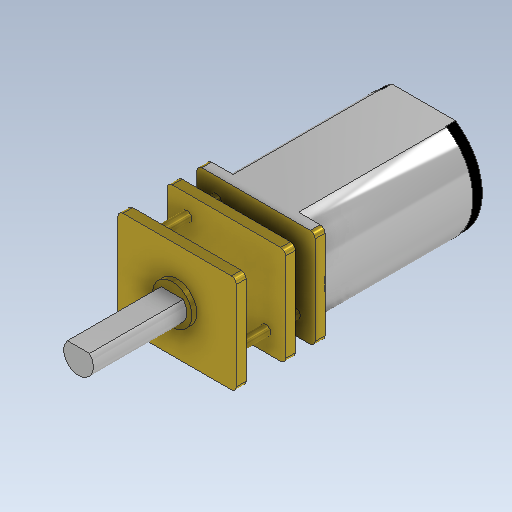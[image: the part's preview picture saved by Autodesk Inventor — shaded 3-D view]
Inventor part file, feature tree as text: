
AUTODESK INVENTOR PART (.ipt)
format: ipt  version: 2020.2 (Build 242310000, 310)  size: 272,896 bytes
history: native  units: mm
features: extrude x11, sketch x10
ambient origin geometry x8: Origin, YZ Plane, XZ Plane, XY Plane, X Axis, Y Axis, Z Axis, Center Point
bodies: Solid1 (feature_tree)
feature tree (21):
  extrude  "Extrusion1"  Depth=5.0mm
  extrude  "Extrusion2"  Depth=15.0mm TaperAngle=0.0deg
  extrude  "Extrusion3"  Depth=0.5mm
  extrude  "Extrusion4"  Depth=4.0mm
  extrude  "Extrusion5"  Depth=3.0mm
  extrude  "Extrusion6"  Depth=1.0mm
  extrude  "Extrusion7"  Depth=2.0mm TaperAngle=0.0deg
  extrude  "Extrusion8"  Depth=1.0mm TaperAngle=0.0deg
  extrude  "Extrusion9"  Depth=0.5mm
  extrude  "Extrusion10"  Depth=3.0mm
  extrude  "Extrusion11"  Depth=1.0mm
  sketch  "Sketch1"  dims[d0=12.0mm d1=5.0mm]
  sketch  "Sketch2"  dims[d2=5.0mm d3=15.0mm d4=0.0mm]
  sketch  "Sketch3"  dims[d5=12.0mm d6=0.5mm]
  sketch  "Sketch4"  dims[d7=1.0mm d8=0.0mm d9=4.0mm]
  sketch  "Sketch5"  dims[d10=3.0mm d11=3.0mm]
  sketch  "Sketch6"  dims[d12=4.0mm d13=1.0mm]
  sketch  "Sketch7"  dims[d14=1.0mm d15=2.0mm d16=0.0mm]
  sketch  "Sketch9"  dims[d17=0.5mm d18=1.0mm d19=0.0mm]
  sketch  "Sketch10"  dims[d20=4.0mm d21=0.0mm d22=0.5mm]
  sketch  "Sketch11"  dims[d23=1.0mm d24=0.0mm d25=3.0mm d26=1.0mm d27=10.0mm d28=0.0mm d30=1.0mm d31=0.0mm d32=10.0mm d33=5.0mm d34=5.0mm d35=11.9mm d36=10.0mm d37=12.0mm d38=0.0mm d39=0.0mm d40=10.0mm d41=12.0mm d42=0.0mm d43=0.0mm d44=5.0mm d45=0.5mm d46=0.0mm d47=1.0mm d48=0.5mm d49=0.0mm d50=4.0mm d51=0.5mm d52=0.0mm]
